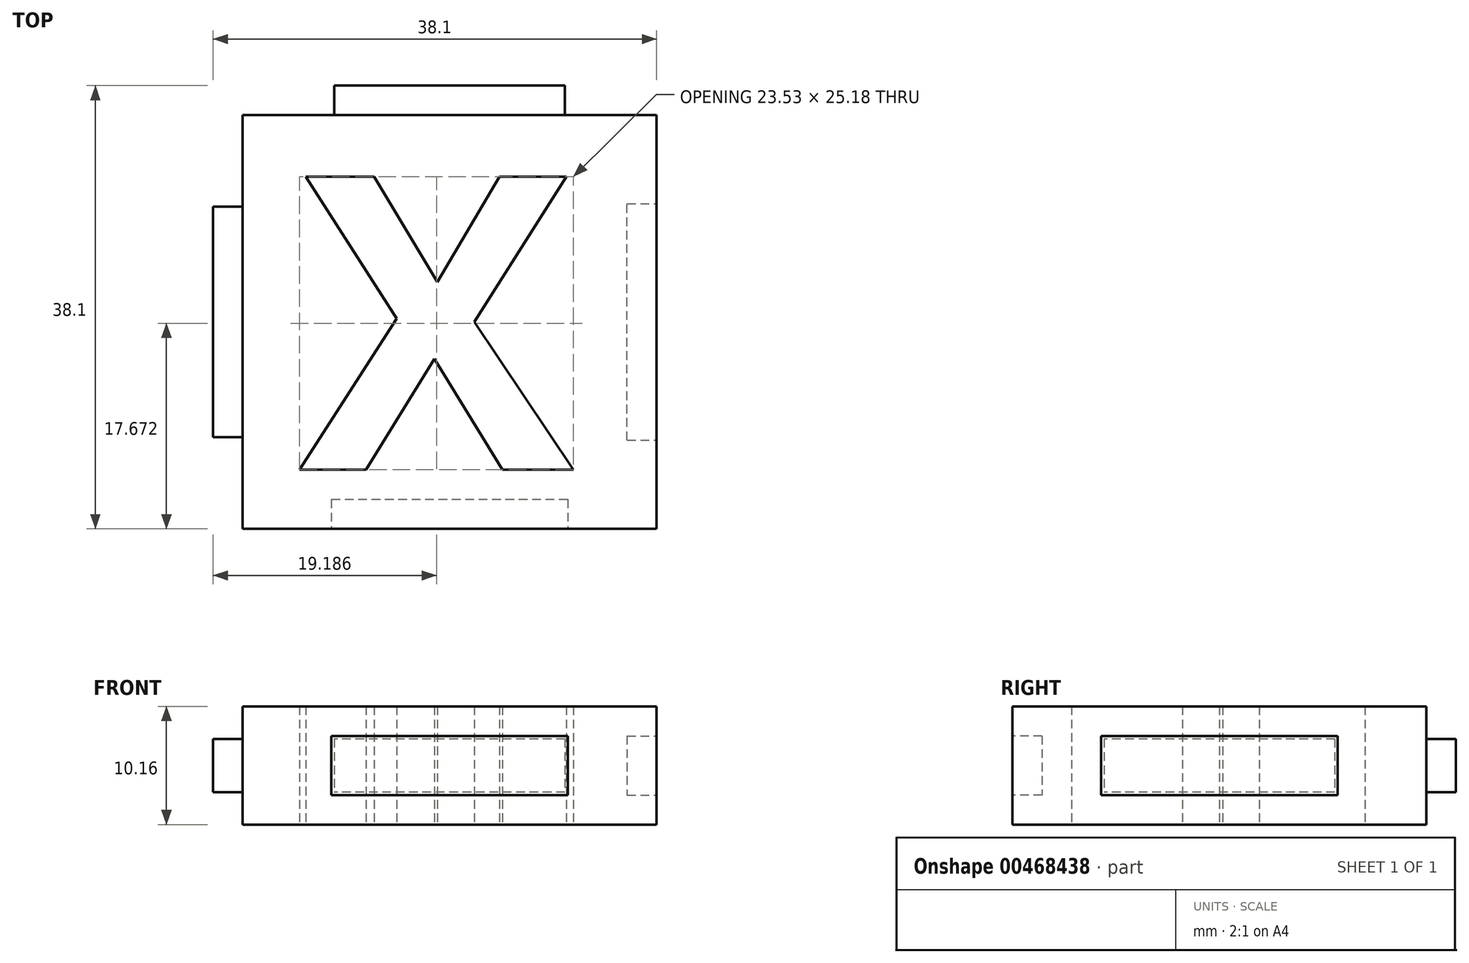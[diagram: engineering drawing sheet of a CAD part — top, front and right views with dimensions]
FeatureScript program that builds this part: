
annotation { "Feature Type Name" : "Feature", "Feature Type Description" : "" }
export const myFeature = defineFeature(function(context is Context, id is Id, definition is map)
    precondition{}
    {
        {
            var Q0;
            Q0=qCreatedBy(makeId("Top.planeOp"),FACE);
            var sketch = newSketch(context, id + "F0", { "sketchPlane" : qUnion([Q0])});
            skLineSegment(sketch, "E0.bottom", {"start": v(-17.78, 17.78) * mm, "end": v(17.78, 17.78) * mm});
            skLineSegment(sketch, "E0.top", {"start": v(-17.78, -17.78) * mm, "end": v(17.78, -17.78) * mm});
            skLineSegment(sketch, "E0.left", {"start": v(-17.78, 17.78) * mm, "end": v(-17.78, -17.78) * mm});
            skLineSegment(sketch, "E0.right", {"start": v(17.78, 17.78) * mm, "end": v(17.78, -17.78) * mm});
            skText(sketch, "E1", { "text": "X", "fontName": "OpenSans-Bold.ttf"});
            const initialGuessF0  = {"E1": [-0.0129, -0.0127, 1, 0, 0.0254]};
            skSetInitialGuess(sketch, initialGuessF0);
            skSolve(sketch);
        }
        {
            var Q0;
            Q0=qSketchRegion(id+"F0",true);
            extrude(context, id + "F1", {"entities" : qUnion([Q0]), "endBound" : BoundingType.SYMMETRIC, "depth" : 10.16 * mm});
        }
        {
            var Q0;
            Q0=makeQuery(id+"F1.opExtrude","SWEPT_FACE",FACE,{"disambiguationData":[OSD([sQuery(id+"F0.wireOp",EDGE,"E0.bottom")])]});
            var sketch = newSketch(context, id + "F2", { "sketchPlane" : qUnion([Q0])});
            skLineSegment(sketch, "E2.bottom", {"start": v(-9.9, 2.29) * mm, "end": v(9.9, 2.29) * mm});
            skLineSegment(sketch, "E2.top", {"start": v(-9.9, -2.29) * mm, "end": v(9.9, -2.29) * mm});
            skLineSegment(sketch, "E2.left", {"start": v(-9.9, 2.29) * mm, "end": v(-9.9, -2.29) * mm});
            skLineSegment(sketch, "E2.right", {"start": v(9.9, 2.29) * mm, "end": v(9.9, -2.29) * mm});
            skSolve(sketch);
        }
        {
            var Q0;
            Q0=qSketchRegion(id+"F2",true);
            extrude(context, id + "F3", {"entities" : qUnion([Q0]), "operationType" : NewBodyOperationType.ADD, "depth" : 2.54 * mm});
        }
        {
            var Q0;
            Q0=makeQuery(id+"F1.opExtrude","SWEPT_FACE",FACE,{"disambiguationData":[OSD([sQuery(id+"F0.wireOp",EDGE,"E0.left")])]});
            var sketch = newSketch(context, id + "F4", { "sketchPlane" : qUnion([Q0])});
            skLineSegment(sketch, "E3.bottom", {"start": v(-9.9, 2.29) * mm, "end": v(9.9, 2.29) * mm});
            skLineSegment(sketch, "E3.top", {"start": v(-9.9, -2.29) * mm, "end": v(9.9, -2.29) * mm});
            skLineSegment(sketch, "E3.left", {"start": v(-9.9, 2.29) * mm, "end": v(-9.9, -2.29) * mm});
            skLineSegment(sketch, "E3.right", {"start": v(9.9, 2.29) * mm, "end": v(9.9, -2.29) * mm});
            skSolve(sketch);
        }
        {
            var Q0;
            Q0=qSketchRegion(id+"F4",true);
            extrude(context, id + "F5", {"entities" : qUnion([Q0]), "operationType" : NewBodyOperationType.ADD, "depth" : 2.54 * mm});
        }
        {
            var Q0;
            Q0=makeQuery(id+"F1.opExtrude","SWEPT_FACE",FACE,{"disambiguationData":[OSD([sQuery(id+"F0.wireOp",EDGE,"E0.top")])]});
            var sketch = newSketch(context, id + "F6", { "sketchPlane" : qUnion([Q0])});
            skLineSegment(sketch, "E4.bottom", {"start": v(-10.16, 2.54) * mm, "end": v(10.16, 2.54) * mm});
            skLineSegment(sketch, "E4.top", {"start": v(-10.16, -2.54) * mm, "end": v(10.16, -2.54) * mm});
            skLineSegment(sketch, "E4.left", {"start": v(-10.16, 2.54) * mm, "end": v(-10.16, -2.54) * mm});
            skLineSegment(sketch, "E4.right", {"start": v(10.16, 2.54) * mm, "end": v(10.16, -2.54) * mm});
            skSolve(sketch);
        }
        {
            var Q0;
            Q0=qSketchRegion(id+"F6",true);
            extrude(context, id + "F7", {"entities" : qUnion([Q0]), "operationType" : NewBodyOperationType.REMOVE, "oppositeDirection" : true, "depth" : 2.54 * mm});
        }
        {
            var Q0;
            Q0=makeQuery(id+"F1.opExtrude","SWEPT_FACE",FACE,{"disambiguationData":[OSD([sQuery(id+"F0.wireOp",EDGE,"E0.right")])]});
            var sketch = newSketch(context, id + "F8", { "sketchPlane" : qUnion([Q0])});
            skLineSegment(sketch, "E5.bottom", {"start": v(-10.16, 2.54) * mm, "end": v(10.16, 2.54) * mm});
            skLineSegment(sketch, "E5.top", {"start": v(-10.16, -2.54) * mm, "end": v(10.16, -2.54) * mm});
            skLineSegment(sketch, "E5.left", {"start": v(-10.16, 2.54) * mm, "end": v(-10.16, -2.54) * mm});
            skLineSegment(sketch, "E5.right", {"start": v(10.16, 2.54) * mm, "end": v(10.16, -2.54) * mm});
            skSolve(sketch);
        }
        {
            var Q0;
            Q0=qSketchRegion(id+"F8",true);
            extrude(context, id + "F9", {"entities" : qUnion([Q0]), "operationType" : NewBodyOperationType.REMOVE, "oppositeDirection" : true, "depth" : 2.54 * mm});
        }
    });
